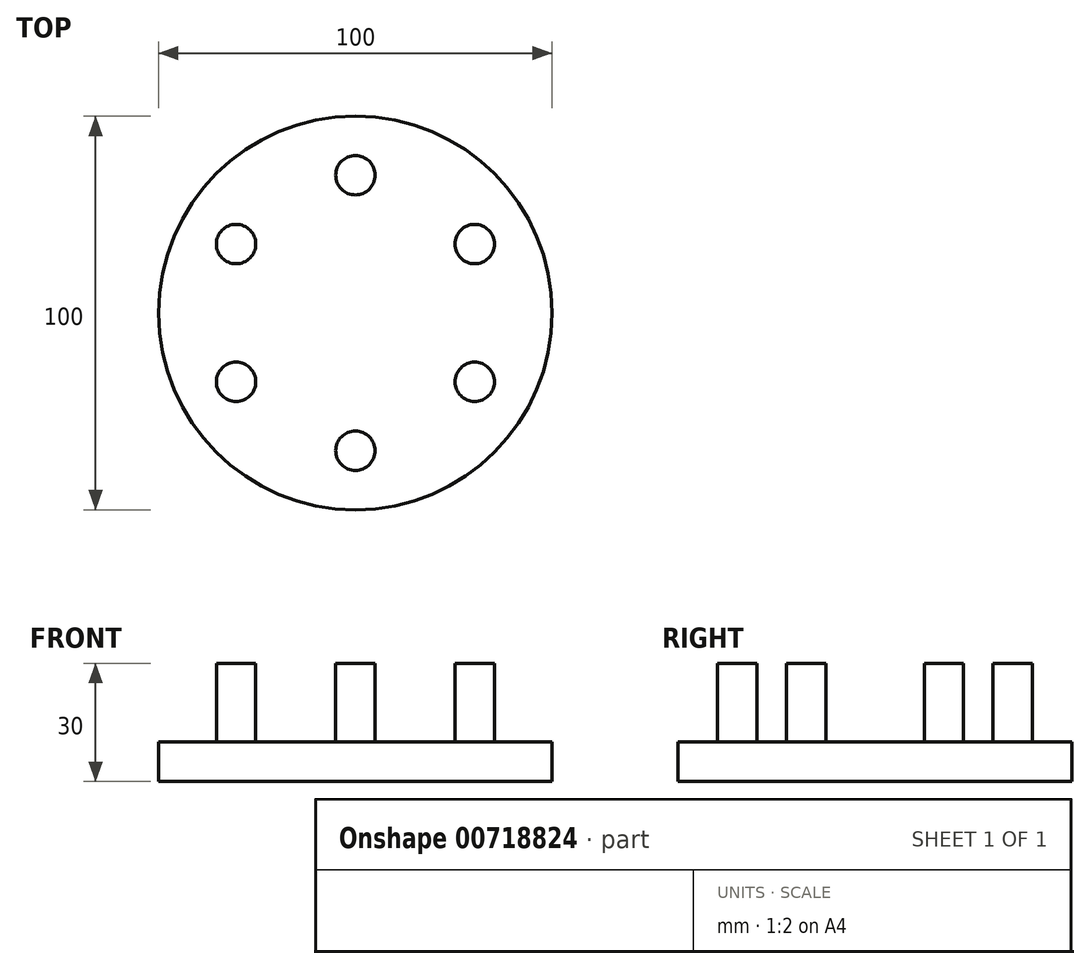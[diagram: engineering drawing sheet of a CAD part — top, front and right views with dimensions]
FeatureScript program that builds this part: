
annotation { "Feature Type Name" : "Feature", "Feature Type Description" : "" }
export const myFeature = defineFeature(function(context is Context, id is Id, definition is map)
    precondition{}
    {
        {
            var Q0;
            Q0=qCreatedBy(makeId("Top.planeOp"),FACE);
            var sketch = newSketch(context, id + "F0", { "sketchPlane" : qUnion([Q0])});
            skCircle(sketch, "E0", {"center": v(0, 0) * mm, "radius": 50 * mm});
            skSolve(sketch);
        }
        {
            var Q0;
            Q0=makeQuery(id+"F0.imprint","IMPRINT",FACE,{"disambiguationData":[TD([[makeQuery(id+"F0.imprint","IMPRINT",EDGE,{"derivedFrom":sQuery(id+"F0.wireOp",EDGE,"E0")}),1.0]])]});
            extrude(context, id + "F1", {"entities" : qUnion([Q0]), "endBound" : BoundingType.SYMMETRIC, "depth" : 10 * mm, "offsetDistance" : 25 * mm});
        }
        {
            var Q0;
            Q0=qCreatedBy(makeId("Top.planeOp"),FACE);
            var sketch = newSketch(context, id + "F2", { "sketchPlane" : qUnion([Q0])});
            skCircle(sketch, "E1", {"center": v(0, 35) * mm, "radius": 5 * mm});
            skPoint(sketch, "E2.center", {"position": v(0, 0) * mm});
            skLineSegment(sketch, "E2.anchor1", {"start": v(0, 0) * mm, "end": v(0, 35) * mm, "construction": true});
            skLineSegment(sketch, "E2.anchor2", {"start": v(0, 0) * mm, "end": v(0, 35) * mm, "construction": true});
            skCircle(sketch, "E3.1.0", {"center": v(-30.31, 17.5) * mm, "radius": 5 * mm});
            skCircle(sketch, "E3.2.0", {"center": v(-30.31, -17.5) * mm, "radius": 5 * mm});
            skCircle(sketch, "E3.3.0", {"center": v(0, -35) * mm, "radius": 5 * mm});
            skCircle(sketch, "E3.4.0", {"center": v(30.31, -17.5) * mm, "radius": 5 * mm});
            skCircle(sketch, "E3.5.0", {"center": v(30.31, 17.5) * mm, "radius": 5 * mm});
            skSolve(sketch);
        }
        {
            var Q0;
            Q0 = qSketchRegion(id + "F2", true);
            extrude(context, id + "F3", {"entities" : qUnion([Q0]), "operationType" : NewBodyOperationType.ADD, "depth" : 25 * mm, "offsetDistance" : 25 * mm});
        }
    });
